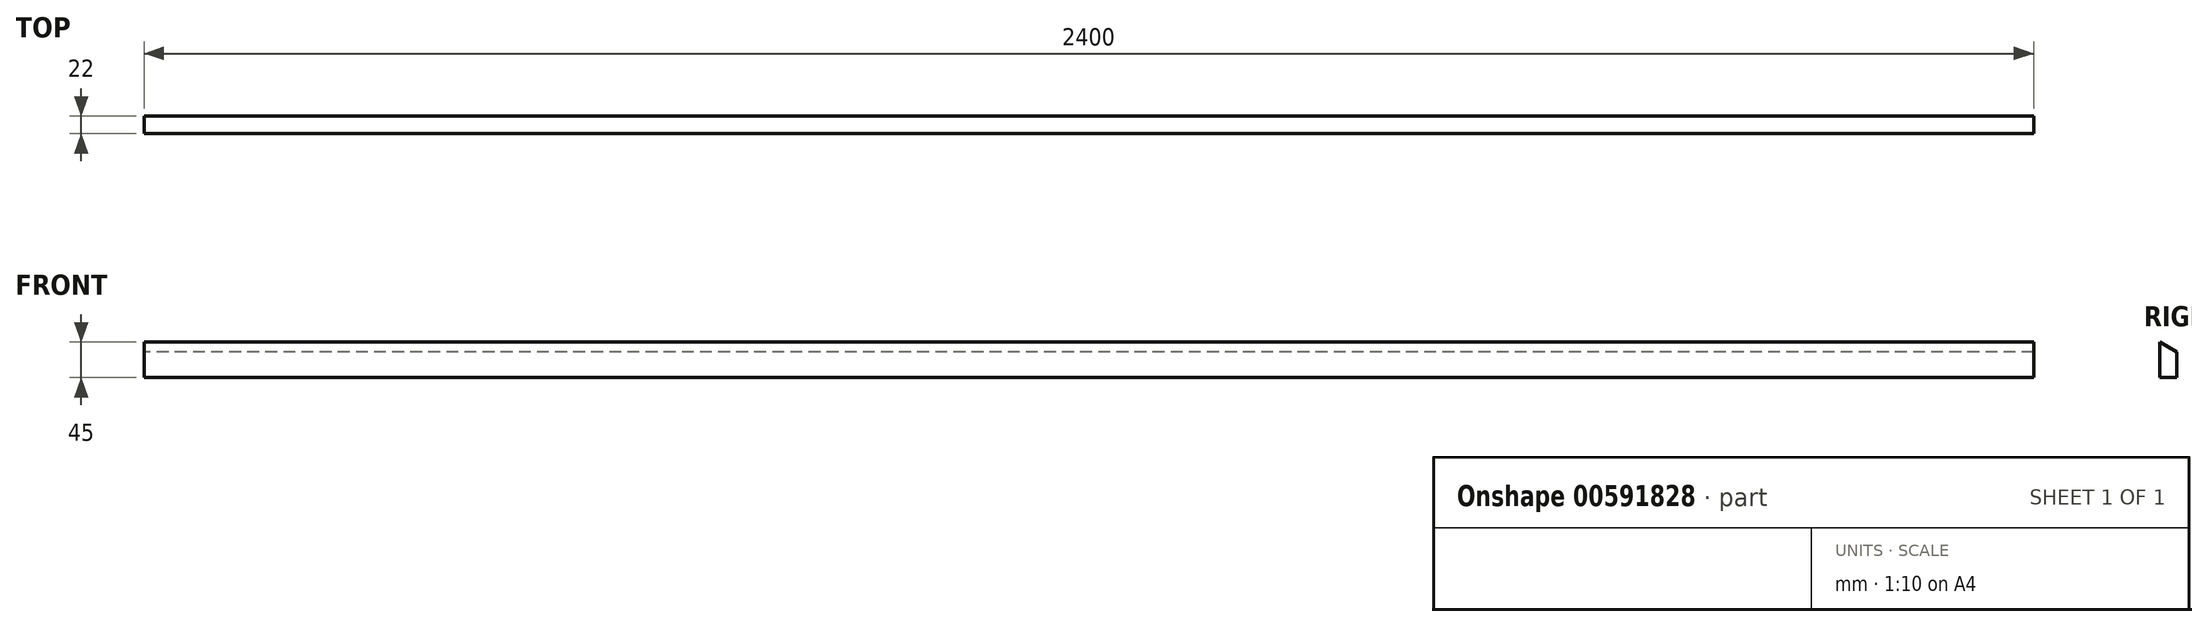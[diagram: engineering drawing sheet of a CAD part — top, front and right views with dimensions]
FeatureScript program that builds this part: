
annotation { "Feature Type Name" : "Feature", "Feature Type Description" : "" }
export const myFeature = defineFeature(function(context is Context, id is Id, definition is map)
    precondition{}
    {
        {
            var Q0;
            Q0=qCreatedBy(makeId("Right.planeOp"),FACE);
            var sketch = newSketch(context, id + "F0", { "sketchPlane" : qUnion([Q0])});
            skLineSegment(sketch, "E0", {"start": v(0, 0) * mm, "end": v(22, 0) * mm});
            skLineSegment(sketch, "E1", {"start": v(22, 0) * mm, "end": v(22, 32.3) * mm});
            skLineSegment(sketch, "E2", {"start": v(22, 32.3) * mm, "end": v(0, 45) * mm});
            skLineSegment(sketch, "E3", {"start": v(0, 45) * mm, "end": v(0, 0) * mm});
            skSolve(sketch);
        }
        {
            var Q0;
            Q0=makeQuery(id+"F0.imprint","IMPRINT",FACE,{"disambiguationData":[TD([[makeQuery(id+"F0.imprint","IMPRINT",EDGE,{"derivedFrom":sQuery(id+"F0.wireOp",EDGE,"E0")}),1.0]])]});
            extrude(context, id + "F1", {"entities" : qUnion([Q0]), "depth" : 2400 * mm, "offsetDistance" : 25 * mm});
        }
    });
